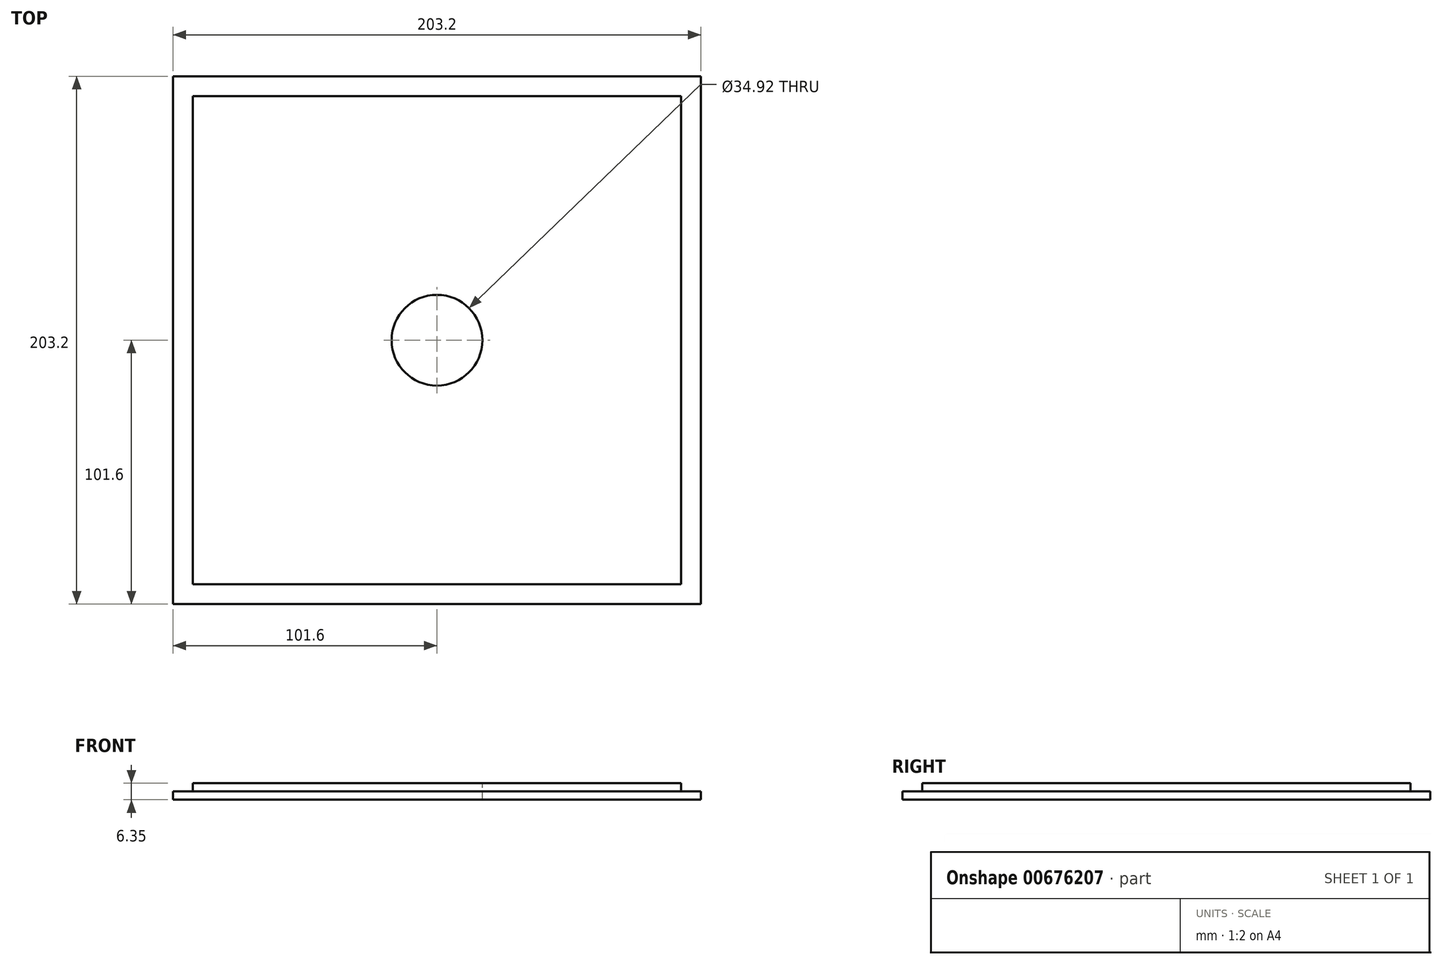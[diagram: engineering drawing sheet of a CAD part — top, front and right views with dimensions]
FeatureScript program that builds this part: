
annotation { "Feature Type Name" : "Feature", "Feature Type Description" : "" }
export const myFeature = defineFeature(function(context is Context, id is Id, definition is map)
    precondition{}
    {
        {
            var Q0;
            Q0=qCreatedBy(makeId("Top.planeOp"),FACE);
            var sketch = newSketch(context, id + "F0", { "sketchPlane" : qUnion([Q0])});
            skLineSegment(sketch, "E0.bottom", {"start": v(-101.6, 101.6) * mm, "end": v(101.6, 101.6) * mm});
            skLineSegment(sketch, "E0.top", {"start": v(-101.6, -101.6) * mm, "end": v(101.6, -101.6) * mm});
            skLineSegment(sketch, "E0.left", {"start": v(-101.6, 101.6) * mm, "end": v(-101.6, -101.6) * mm});
            skLineSegment(sketch, "E0.right", {"start": v(101.6, 101.6) * mm, "end": v(101.6, -101.6) * mm});
            skPoint(sketch, "E0.middle", {"position": v(0, 0) * mm});
            skSolve(sketch);
        }
        {
            var Q0;
            Q0 = qSketchRegion(id + "F0", true);
            extrude(context, id + "F1", {"entities" : qUnion([Q0]), "depth" : 3.17 * mm, "offsetDistance" : 25.4 * mm});
        }
        {
            var Q0;
            Q0=makeQuery(id+"F1.opExtrude","CAP_FACE",FACE,{"disambiguationData":[OSD([sQuery(id+"F0.wireOp",EDGE,"E0.bottom"),sQuery(id+"F0.wireOp",EDGE,"E0.top"),sQuery(id+"F0.wireOp",EDGE,"E0.left"),sQuery(id+"F0.wireOp",EDGE,"E0.right")])],"isStart":false});
            var sketch = newSketch(context, id + "F2", { "sketchPlane" : qUnion([Q0])});
            skLineSegment(sketch, "E1.bottom", {"start": v(-93.98, 93.98) * mm, "end": v(93.98, 93.98) * mm});
            skLineSegment(sketch, "E1.top", {"start": v(-93.98, -93.98) * mm, "end": v(93.98, -93.98) * mm});
            skLineSegment(sketch, "E1.left", {"start": v(-93.98, 93.98) * mm, "end": v(-93.98, -93.98) * mm});
            skLineSegment(sketch, "E1.right", {"start": v(93.98, 93.98) * mm, "end": v(93.98, -93.98) * mm});
            skPoint(sketch, "E1.middle", {"position": v(0, 0) * mm});
            skSolve(sketch);
        }
        {
            var Q0;
            Q0 = qSketchRegion(id + "F2", true);
            extrude(context, id + "F3", {"entities" : qUnion([Q0]), "operationType" : NewBodyOperationType.ADD, "depth" : 3.17 * mm, "offsetDistance" : 25.4 * mm});
        }
        {
            var Q0;
            Q0=makeQuery(id+"F3.opExtrude","CAP_FACE",FACE,{"disambiguationData":[OSD([sQuery(id+"F2.wireOp",EDGE,"E1.bottom"),sQuery(id+"F2.wireOp",EDGE,"E1.top"),sQuery(id+"F2.wireOp",EDGE,"E1.left"),sQuery(id+"F2.wireOp",EDGE,"E1.right")])],"isStart":false});
            var sketch = newSketch(context, id + "F4", { "sketchPlane" : qUnion([Q0])});
            skCircle(sketch, "E2", {"center": v(0, 0) * mm, "radius": 17.46 * mm});
            skSolve(sketch);
        }
        {
            var Q0;
            Q0 = qSketchRegion(id + "F4", true);
            extrude(context, id + "F5", {"entities" : qUnion([Q0]), "operationType" : NewBodyOperationType.REMOVE, "oppositeDirection" : true, "depth" : 25.4 * mm, "offsetDistance" : 25.4 * mm});
        }
    });
